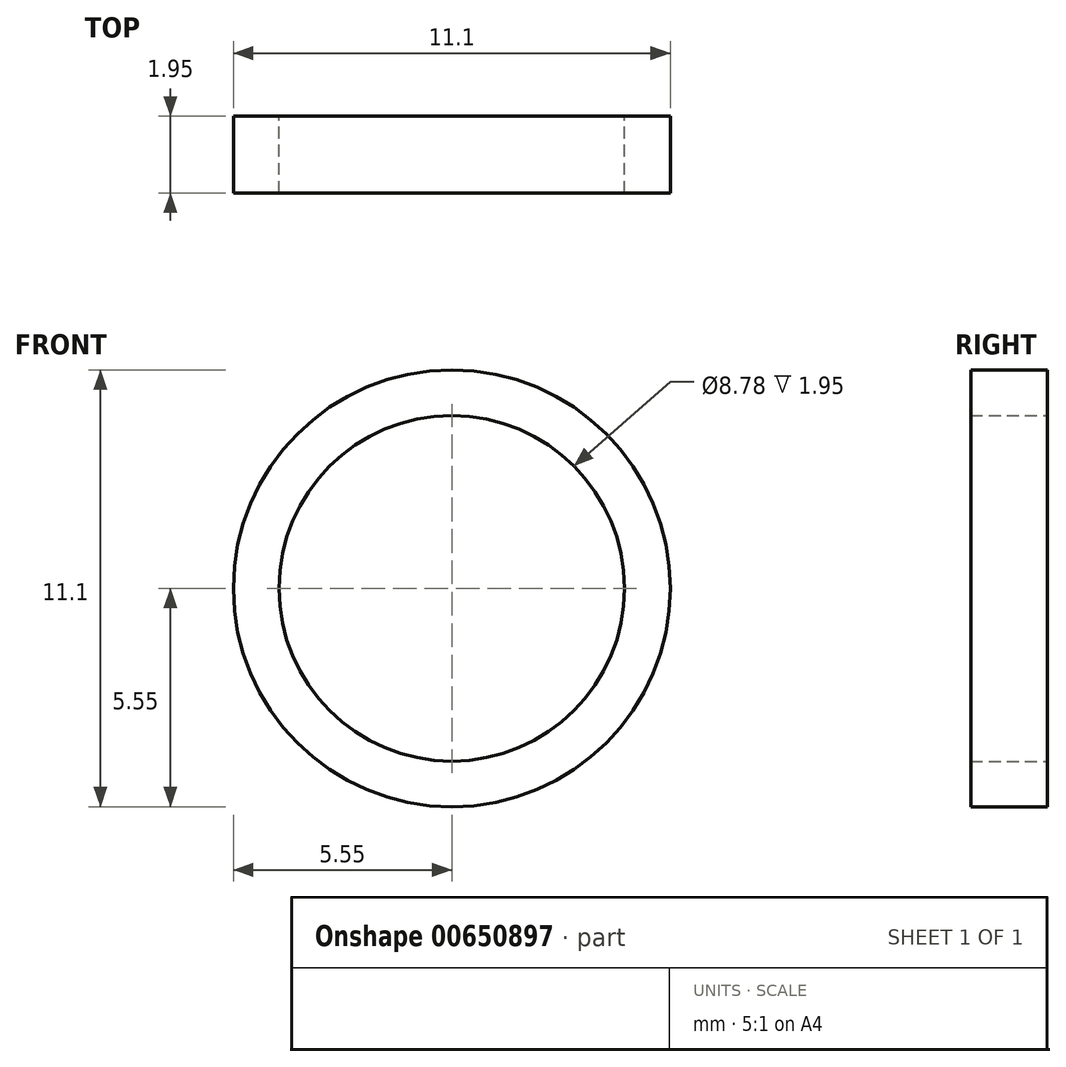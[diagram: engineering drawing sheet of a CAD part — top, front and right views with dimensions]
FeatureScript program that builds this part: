
annotation { "Feature Type Name" : "Feature", "Feature Type Description" : "" }
export const myFeature = defineFeature(function(context is Context, id is Id, definition is map)
    precondition{}
    {
        {
            var Q0;
            Q0=qCreatedBy(makeId("Front.planeOp"),FACE);
            var sketch = newSketch(context, id + "F0", { "sketchPlane" : qUnion([Q0])});
            skCircle(sketch, "E0", {"center": v(0, 0) * mm, "radius": 5.55 * mm});
            skSolve(sketch);
        }
        {
            var Q0;
            Q0=qCreatedBy(makeId("Front.planeOp"),FACE);
            var sketch = newSketch(context, id + "F1", { "sketchPlane" : qUnion([Q0])});
            skCircle(sketch, "E1", {"center": v(0, 0) * mm, "radius": 4.39 * mm});
            skSolve(sketch);
        }
        {
            var Q0;
            Q0 = qSketchRegion(id + "F0", true);
            extrude(context, id + "F2", {"entities" : qUnion([Q0]), "depth" : 1.95 * mm, "offsetDistance" : 25 * mm});
        }
        {
            var Q0;
            Q0=sQuery(id+"F1.wireOp",VERTEX,"E1.center");
            var Q1;
            Q1=makeQuery(id+"F2.opExtrude","SWEPT_BODY",BODY,{"disambiguationData":[OSD([sQuery(id+"F0.wireOp",EDGE,"E0")])]});
            hole(context, id + "F3", {"style" : HoleStyle.SIMPLE, "endStyle" : HoleEndStyle.THROUGH, "oppositeDirection" : true, "holeDiameter" : 8.78 * mm, "majorDiameter" : 5 * mm, "isTappedThrough" : true, "tappedDepth" : 12 * mm, "tapClearance" : 3, "locations" : qUnion([Q0]), "scope" : qUnion([Q1])});
        }
    });
